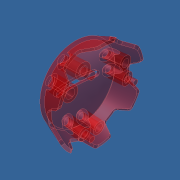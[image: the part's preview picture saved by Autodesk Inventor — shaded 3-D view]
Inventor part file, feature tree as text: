
AUTODESK INVENTOR PART (.ipt)
format: ipt  version: unknown  size: 463,872 bytes
history: native  units: mm
features: sketch x5, extrude x4, pattern_circular x2, revolve x1, fillet x1, other x1
ambient origin geometry x8: Origin, YZ Plane, XZ Plane, XY Plane, X Axis, Y Axis, Z Axis, Center Point
feature tree (14):
  revolve  "Вращение1"
  extrude  "Выдавливание2"  Depth=12.8mm
  fillet  "Сопряжение1"  Radius=45.6mm
  pattern_circular  "Круговой массив1"  [2 undecoded]
  extrude  "Выдавливание3"  Depth=16.7mm
  other  "РабПлоскость10"
  extrude  "Выдавливание4"  Depth=1.4mm
  extrude  "Выдавливание5"  Depth=1.4mm
  pattern_circular  "Круговой массив2"  [2 undecoded]
  sketch  "Эскиз1"
  sketch  "Эскиз2"
  sketch  "Эскиз3"
  sketch  "Эскиз8"
  sketch  "Эскиз9"
note: 4 required parameter values undecoded (feature->parameter linkage not recoverable at this tier; creation-order binding heuristic only, values carry confidence <= 0.55)
